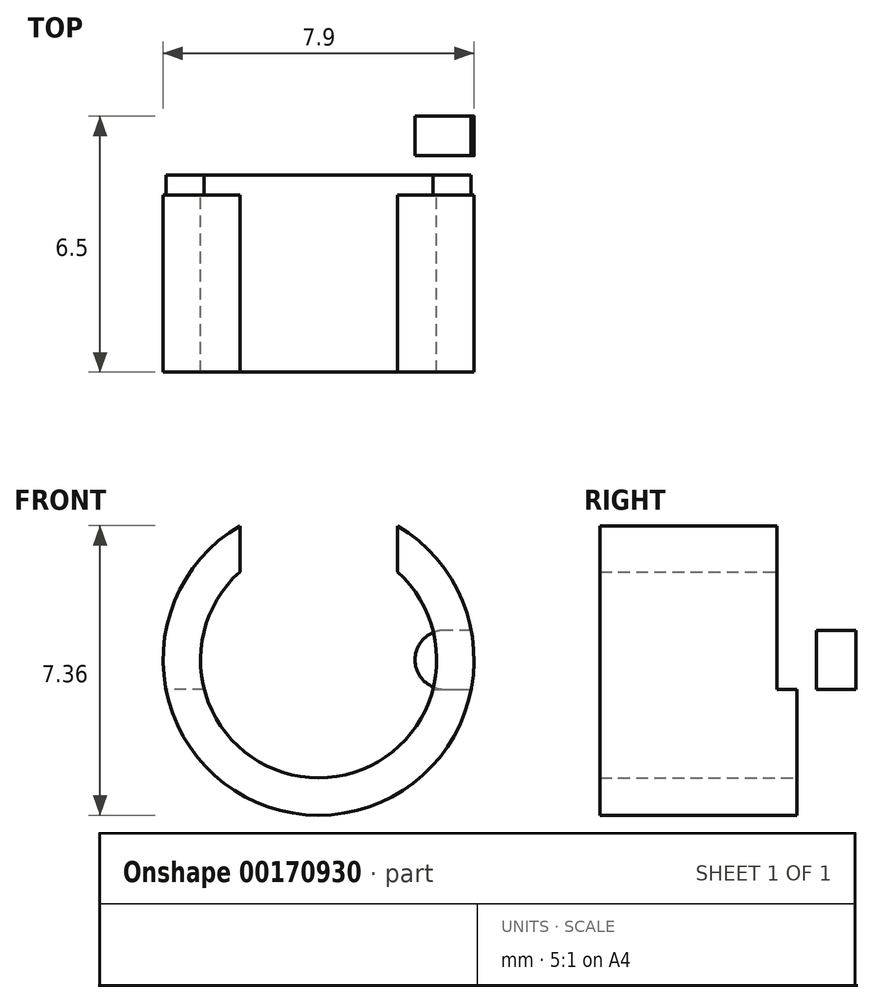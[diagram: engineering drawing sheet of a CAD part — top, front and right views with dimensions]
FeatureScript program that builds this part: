
annotation { "Feature Type Name" : "Feature", "Feature Type Description" : "" }
export const myFeature = defineFeature(function(context is Context, id is Id, definition is map)
    precondition{}
    {
        {
            assignVariable(context, id + "F0", {"name" : "Main_Diam", "anyValue" : 7.9});
        }
        {
            assignVariable(context, id + "F1", {"name" : "Main_Length", "anyValue" : 6.5});
        }
        {
            assignVariable(context, id + "F2", {"name" : "Relief2_Size", "anyValue" : 1});
        }
        {
            assignVariable(context, id + "F3", {"name" : "Cap_Thickness", "anyValue" : 1});
        }
        {
            var Q0;
            Q0=qCreatedBy(makeId("Front.planeOp"),FACE);
            var sketch = newSketch(context, id + "F4", { "sketchPlane" : qUnion([Q0])});
            skCircle(sketch, "E0", {"center": v(0, 0) * mm, "radius": 3.95 * mm});
            skCircle(sketch, "E1", {"center": v(0, 0) * mm, "radius": 3 * mm});
            skSolve(sketch);
        }
        {
            var Q0;
            Q0=makeQuery(id+"F4.imprint","IMPRINT",FACE,{"disambiguationData":[TD([[makeQuery(id+"F4.imprint","IMPRINT",EDGE,{"derivedFrom":sQuery(id+"F4.wireOp",EDGE,"E0")}),1.0]])]});
            extrude(context, id + "F5", {"entities" : qUnion([Q0]), "depth" : (getVariable(context, 'Main_Length')) * mm});
        }
        {
            var Q0;
            Q0=makeQuery(id+"F4.imprint","IMPRINT",FACE,{"disambiguationData":[TD([[makeQuery(id+"F4.imprint","IMPRINT",EDGE,{"derivedFrom":sQuery(id+"F4.wireOp",EDGE,"E1")}),1.0]])]});
            extrude(context, id + "F6", {"entities" : qUnion([Q0]), "operationType" : NewBodyOperationType.ADD, "depth" : (getVariable(context, 'Cap_Thickness')) * mm});
        }
        {
            var Q0;
            Q0=qCreatedBy(makeId("Top.planeOp"),FACE);
            var sketch = newSketch(context, id + "F7", { "sketchPlane" : qUnion([Q0])});
            skLineSegment(sketch, "E2", {"start": v(-2, -1) * mm, "end": v(-2, -6.5) * mm});
            skLineSegment(sketch, "E3", {"start": v(2, -1) * mm, "end": v(2, -6.5) * mm});
            skLineSegment(sketch, "E4.0", {"start": v(3.95, -6.5) * mm, "end": v(-3.95, -6.5) * mm});
            skLineSegment(sketch, "E5.0", {"start": v(3, -1) * mm, "end": v(-3, -1) * mm});
            skSolve(sketch);
        }
        {
            var Q0;
            {var subQ0=sQuery(id+"F7.wireOp",EDGE,"E2");Q0=makeQuery(id+"F7.imprint","IMPRINT",FACE,{"disambiguationData":[TD([[makeQuery(id+"F7.imprint","IMPRINT",EDGE,{"derivedFrom":subQ0}),1.0]])]});}
            extrude(context, id + "F8", {"entities" : qUnion([Q0]), "operationType" : NewBodyOperationType.REMOVE, "endBound" : BoundingType.THROUGH_ALL, "depth" : 25 * mm});
        }
        {
            var Q0;
            {var subQ0=sQuery(id+"F4.wireOp",EDGE,"E1");Q0=makeQuery(id+"F6.boolean.opBoolean","MERGE",FACE,{"derivedFrom":[makeQuery(id+"F5.opExtrude","CAP_FACE",FACE,{"disambiguationData":[OSD([sQuery(id+"F4.wireOp",EDGE,"E0"),subQ0])],"isStart":true}),makeQuery(id+"F6.opExtrude","CAP_FACE",FACE,{"disambiguationData":[OSD([subQ0])],"isStart":true})]});}
            var sketch = newSketch(context, id + "F9", { "sketchPlane" : qUnion([Q0])});
            skLineSegment(sketch, "E6", {"start": v(3.88, 0.75) * mm, "end": v(3.2, 0.75) * mm});
            skArc(sketch, "E7", {"start": v(3.2, 0.75) * mm, "mid": v(2.45, 0) * mm, "end": v(3.2, -0.75) * mm});
            skLineSegment(sketch, "E8", {"start": v(3.2, -0.75) * mm, "end": v(3.88, -0.75) * mm});
            skLineSegment(sketch, "E9", {"start": v(0, 0) * mm, "end": v(0, 3.95) * mm, "construction": true});
            skArc(sketch, "E10.MirrorCS", {"start": v(-3.2, 0.75) * mm, "mid": v(-2.45, 0) * mm, "end": v(-3.2, -0.75) * mm});
            skLineSegment(sketch, "E11.MirrorCS", {"start": v(-3.88, 0.75) * mm, "end": v(-3.2, 0.75) * mm});
            skLineSegment(sketch, "E12.MirrorCS", {"start": v(-3.2, -0.75) * mm, "end": v(-3.88, -0.75) * mm});
            skSolve(sketch);
        }
        {
            var Q0;
            Q0=makeQuery(id+"F9.imprint","IMPRINT",FACE,{"disambiguationData":[TD([[makeQuery(id+"F9.imprint","IMPRINT",EDGE,{"derivedFrom":sQuery(id+"F9.wireOp",EDGE,"E10.MirrorCS")}),-1.0]])]});
            var Q1;
            {var subQ0=sQuery(id+"F9.wireOp",EDGE,"E6");Q1=makeQuery(id+"F9.imprint","IMPRINT",FACE,{"disambiguationData":[TD([[makeQuery(id+"F9.imprint","IMPRINT",EDGE,{"derivedFrom":subQ0}),1.0]])]});}
            extrude(context, id + "F10", {"entities" : qUnion([Q0, Q1]), "operationType" : NewBodyOperationType.REMOVE, "oppositeDirection" : true, "depth" : (getVariable(context, 'Cap_Thickness') + getVariable(context, 'Relief2_Size') / 2) * mm});
        }
        {
            var Q0;
            Q0=qCreatedBy(makeId("Right.planeOp"),FACE);
            cPlane(context, id + "F11", {"entities" : qUnion([Q0]), "cplaneType" : CPlaneType.OFFSET, "offset" : (getVariable(context, 'Main_Diam') / 2) * mm, "width" : 150 * mm, "height" : 150 * mm});
        }
        {
            var Q0;
            Q0=qCreatedBy(id+"F11.planeOp",FACE);
            var sketch = newSketch(context, id + "F12", { "sketchPlane" : qUnion([Q0])});
            skLineSegment(sketch, "E13", {"start": v(-2, 3.95) * mm, "end": v(-2, -0.75) * mm});
            skLineSegment(sketch, "E14", {"start": v(-1, -0.75) * mm, "end": v(-1, 3.95) * mm});
            skLineSegment(sketch, "E15", {"start": v(-2, 3.95) * mm, "end": v(-1, 3.95) * mm});
            skLineSegment(sketch, "E16.0", {"start": v(0, -3.95) * mm, "end": v(0, 3.95) * mm});
            skLineSegment(sketch, "E17", {"start": v(-2, -0.75) * mm, "end": v(-1, -0.75) * mm});
            skSolve(sketch);
        }
        {
            var Q0;
            Q0=makeQuery(id+"F12.imprint","IMPRINT",FACE,{"disambiguationData":[TD([[makeQuery(id+"F12.imprint","IMPRINT",EDGE,{"derivedFrom":sQuery(id+"F12.wireOp",EDGE,"E13")}),1.0]])]});
            extrude(context, id + "F13", {"entities" : qUnion([Q0]), "operationType" : NewBodyOperationType.REMOVE, "endBound" : BoundingType.THROUGH_ALL, "oppositeDirection" : true, "depth" : 25 * mm});
        }
    });
